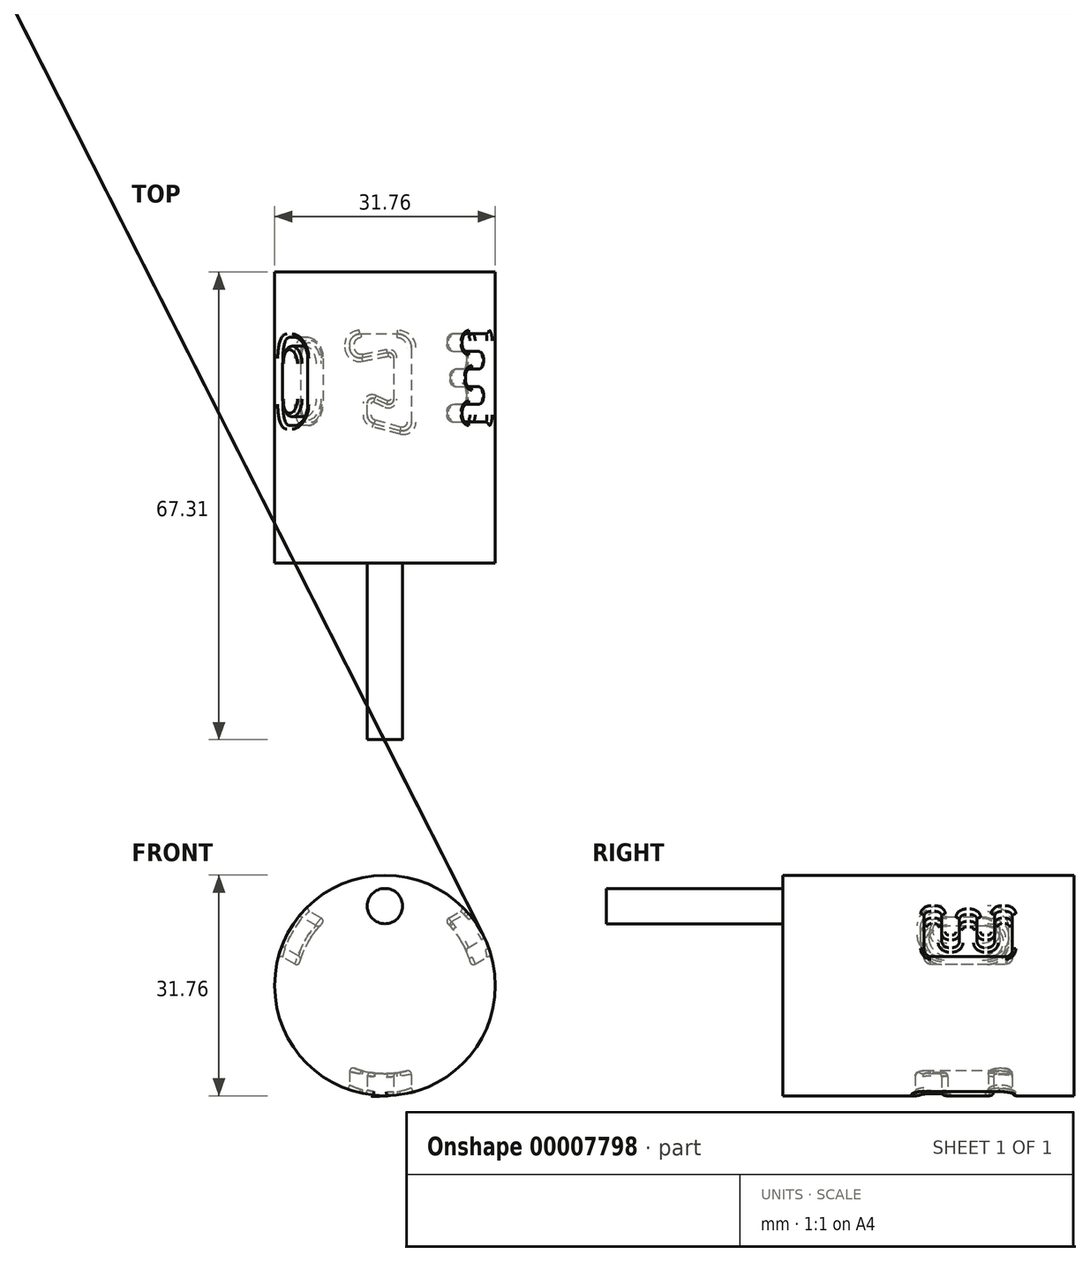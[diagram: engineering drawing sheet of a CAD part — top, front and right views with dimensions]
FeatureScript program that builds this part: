
annotation { "Feature Type Name" : "Feature", "Feature Type Description" : "" }
export const myFeature = defineFeature(function(context is Context, id is Id, definition is map)
    precondition{}
    {
        {
            var Q0;
            Q0=qCreatedBy(makeId("Front.planeOp"),FACE);
            var sketch = newSketch(context, id + "F0", { "sketchPlane" : qUnion([Q0])});
            skCircle(sketch, "E0", {"center": v(0, 0) * mm, "radius": 15.88 * mm});
            skSolve(sketch);
        }
        {
            var Q0;
            Q0 = qSketchRegion(id + "F0", true);
            extrude(context, id + "F1", {"entities" : qUnion([Q0]), "depth" : 38.1 * mm});
        }
        {
            var Q0;
            Q0=qCreatedBy(makeId("Top.planeOp"),FACE);
            var sketch = newSketch(context, id + "F2", { "sketchPlane" : qUnion([Q0])});
            skLineSegment(sketch, "E1", {"start": v(-7.62, -35.56) * mm, "end": v(0, -24.13) * mm});
            skLineSegment(sketch, "E2", {"start": v(0, -24.13) * mm, "end": v(7.62, -35.56) * mm});
            skLineSegment(sketch, "E3", {"start": v(-8.9, -5.08) * mm, "end": v(-8.9, 0) * mm});
            skLineSegment(sketch, "E4", {"start": v(-8.9, 0) * mm, "end": v(0, -5.08) * mm});
            skLineSegment(sketch, "E5", {"start": v(0, -5.08) * mm, "end": v(8.89, 0) * mm});
            skLineSegment(sketch, "E6", {"start": v(8.9, 0) * mm, "end": v(8.9, -5.08) * mm});
            skArc(sketch, "E7", {"start": v(-8.9, -15.24) * mm, "mid": v(-10.64, -25.55) * mm, "end": v(-7.62, -35.56) * mm});
            skArc(sketch, "E8", {"start": v(7.62, -35.56) * mm, "mid": v(10.64, -25.55) * mm, "end": v(8.9, -15.24) * mm});
            skArc(sketch, "E9", {"start": v(8.9, -15.24) * mm, "mid": v(12.14, -9.84) * mm, "end": v(13.97, -3.8) * mm});
            skArc(sketch, "E10", {"start": v(-13.97, -3.81) * mm, "mid": v(-12.14, -9.84) * mm, "end": v(-8.9, -15.24) * mm});
            skLineSegment(sketch, "E11", {"start": v(8.9, -5.08) * mm, "end": v(13.97, -3.8) * mm});
            skLineSegment(sketch, "E12", {"start": v(-13.97, -3.81) * mm, "end": v(-8.9, -5.08) * mm});
            skLineSegment(sketch, "E13", {"start": v(0, -24.13) * mm, "end": v(0, -5.08) * mm});
            skSolve(sketch);
        }
        {
            var Q0;
            Q0=qCreatedBy(makeId("Top.planeOp"),FACE);
            cPlane(context, id + "F3", {"entities" : qUnion([Q0]), "cplaneType" : CPlaneType.OFFSET, "offset" : 15.88 * mm, "oppositeDirection" : true, "width" : 152.4 * mm, "height" : 152.4 * mm});
        }
        {
            var Q0;
            Q0=qCreatedBy(id+"F3.planeOp",FACE);
            var sketch = newSketch(context, id + "F4", { "sketchPlane" : qUnion([Q0])});
            skLineSegment(sketch, "E14", {"start": v(3.81, -21.59) * mm, "end": v(3.8, -10.92) * mm});
            skLineSegment(sketch, "E15", {"start": v(1.78, -8.9) * mm, "end": v(-3.56, -8.9) * mm});
            skPoint(sketch, "E16.visualSharp", {"position": v(3.81, -21.59) * mm});
            skPoint(sketch, "E17.visualSharp", {"position": v(3.8, -8.9) * mm});
            skArc(sketch, "E17.filletArc", {"start": v(3.81, -10.92) * mm, "mid": v(3.21, -9.49) * mm, "end": v(1.78, -8.9) * mm});
            skLineSegment(sketch, "E18", {"start": v(-5.08, -10.41) * mm, "end": v(-5.08, -10.84) * mm});
            skLineSegment(sketch, "E19", {"start": v(-3.26, -12.34) * mm, "end": v(0.36, -11.61) * mm});
            skLineSegment(sketch, "E20", {"start": v(1.27, -12.36) * mm, "end": v(1.27, -18.29) * mm});
            skPoint(sketch, "E21.visualSharp", {"position": v(-5.08, -12.7) * mm});
            skArc(sketch, "E21.filletArc", {"start": v(-5.08, -10.84) * mm, "mid": v(-4.52, -12.02) * mm, "end": v(-3.26, -12.34) * mm});
            skPoint(sketch, "E22.visualSharp", {"position": v(-5.08, -8.9) * mm});
            skArc(sketch, "E22.filletArc", {"start": v(-3.56, -8.89) * mm, "mid": v(-4.63, -9.34) * mm, "end": v(-5.08, -10.41) * mm});
            skPoint(sketch, "E23.visualSharp", {"position": v(1.27, -11.43) * mm});
            skArc(sketch, "E23.filletArc", {"start": v(1.27, -12.36) * mm, "mid": v(1, -11.77) * mm, "end": v(0.36, -11.61) * mm});
            skLineSegment(sketch, "E24", {"start": v(2.21, -22.82) * mm, "end": v(-1.6, -21.8) * mm});
            skLineSegment(sketch, "E25", {"start": v(-2.54, -20.57) * mm, "end": v(-2.54, -18.92) * mm});
            skLineSegment(sketch, "E26", {"start": v(-1.46, -18.23) * mm, "end": v(0.2, -18.98) * mm});
            skArc(sketch, "E27.filletArc", {"start": v(2.21, -22.82) * mm, "mid": v(3.31, -22.6) * mm, "end": v(3.81, -21.59) * mm});
            skPoint(sketch, "E28.visualSharp", {"position": v(-2.54, -21.54) * mm});
            skArc(sketch, "E28.filletArc", {"start": v(-2.54, -20.57) * mm, "mid": v(-2.28, -21.34) * mm, "end": v(-1.6, -21.8) * mm});
            skPoint(sketch, "E29.visualSharp", {"position": v(-2.54, -17.73) * mm});
            skArc(sketch, "E29.filletArc", {"start": v(-1.46, -18.23) * mm, "mid": v(-2.2, -18.28) * mm, "end": v(-2.54, -18.92) * mm});
            skPoint(sketch, "E30.visualSharp", {"position": v(1.27, -19.47) * mm});
            skArc(sketch, "E30.filletArc", {"start": v(0.2, -18.98) * mm, "mid": v(0.92, -18.93) * mm, "end": v(1.27, -18.29) * mm});
            skSolve(sketch);
        }
        {
            var Q0;
            Q0 = qSketchRegion(id + "F4", true);
            extrude(context, id + "F5", {"entities" : qUnion([Q0]), "depth" : 25.4 * mm});
        }
        {
            var Q0;
            Q0=makeQuery(id+"F1.opExtrude","CAP_FACE",FACE,{"disambiguationData":[OSD([sQuery(id+"F0.wireOp",EDGE,"E0")])],"isStart":false});
            var sketch = newSketch(context, id + "F6", { "sketchPlane" : qUnion([Q0])});
            skCircle(sketch, "E31", {"center": v(0, 0) * mm, "radius": 12.7 * mm});
            skSolve(sketch);
        }
        {
            var Q0;
            Q0 = qSketchRegion(id + "F6", true);
            extrude(context, id + "F7", {"entities" : qUnion([Q0]), "oppositeDirection" : true, "depth" : 38.1 * mm});
        }
        {
            var Q0;
            Q0=makeQuery(id+"F7.opExtrude","SWEPT_BODY",BODY,{"disambiguationData":[OSD([sQuery(id+"F6.wireOp",EDGE,"E31")])]});
            var Q1;
            Q1=makeQuery(id+"F5.opExtrude","SWEPT_BODY",BODY,{"disambiguationData":[OSD([sQuery(id+"F4.wireOp",EDGE,"E14"),sQuery(id+"F4.wireOp",EDGE,"E15"),sQuery(id+"F4.wireOp",EDGE,"E17.filletArc"),sQuery(id+"F4.wireOp",EDGE,"E18"),sQuery(id+"F4.wireOp",EDGE,"E19"),sQuery(id+"F4.wireOp",EDGE,"E20"),sQuery(id+"F4.wireOp",EDGE,"E21.filletArc"),sQuery(id+"F4.wireOp",EDGE,"E22.filletArc"),sQuery(id+"F4.wireOp",EDGE,"E23.filletArc"),sQuery(id+"F4.wireOp",EDGE,"E24"),sQuery(id+"F4.wireOp",EDGE,"E25"),sQuery(id+"F4.wireOp",EDGE,"E26"),sQuery(id+"F4.wireOp",EDGE,"E27.filletArc"),sQuery(id+"F4.wireOp",EDGE,"E28.filletArc"),sQuery(id+"F4.wireOp",EDGE,"E29.filletArc"),sQuery(id+"F4.wireOp",EDGE,"E30.filletArc")])]});
            booleanBodies(context, id + "F8", {"operationType" : BooleanOperationType.SUBTRACTION, "tools" : qUnion([Q0]), "targets" : qUnion([Q1]), "keepTools" : true});
        }
        {
            var Q0;
            Q0=makeQuery(id+"F5.opExtrude","SWEPT_BODY",BODY,{"disambiguationData":[OSD([sQuery(id+"F4.wireOp",EDGE,"E14"),sQuery(id+"F4.wireOp",EDGE,"E15"),sQuery(id+"F4.wireOp",EDGE,"E17.filletArc"),sQuery(id+"F4.wireOp",EDGE,"E18"),sQuery(id+"F4.wireOp",EDGE,"E19"),sQuery(id+"F4.wireOp",EDGE,"E20"),sQuery(id+"F4.wireOp",EDGE,"E21.filletArc"),sQuery(id+"F4.wireOp",EDGE,"E22.filletArc"),sQuery(id+"F4.wireOp",EDGE,"E23.filletArc"),sQuery(id+"F4.wireOp",EDGE,"E24"),sQuery(id+"F4.wireOp",EDGE,"E25"),sQuery(id+"F4.wireOp",EDGE,"E26"),sQuery(id+"F4.wireOp",EDGE,"E27.filletArc"),sQuery(id+"F4.wireOp",EDGE,"E28.filletArc"),sQuery(id+"F4.wireOp",EDGE,"E29.filletArc"),sQuery(id+"F4.wireOp",EDGE,"E30.filletArc")])]});
            var Q1;
            Q1=makeQuery(id+"F1.opExtrude","SWEPT_BODY",BODY,{"disambiguationData":[OSD([sQuery(id+"F0.wireOp",EDGE,"E0")])]});
            booleanBodies(context, id + "F9", {"operationType" : BooleanOperationType.SUBTRACTION, "tools" : qUnion([Q0]), "targets" : qUnion([Q1])});
        }
        {
            var Q0;
            Q0=makeQuery(id+"F9.opBoolean","COPY",EDGE,{"derivedFrom":makeQuery(id+"F8.opBoolean","INTERSECT",EDGE,{"derivedFrom":[makeQuery(id+"F5.opExtrude","SWEPT_FACE",FACE,{"disambiguationData":[OSD([sQuery(id+"F4.wireOp",EDGE,"E20")])]}),makeQuery(id+"F7.opExtrude","SWEPT_FACE",FACE,{"disambiguationData":[OSD([sQuery(id+"F6.wireOp",EDGE,"E31")])]})]})});
            var Q1;
            Q1=makeQuery(id+"F9.opBoolean","COPY",EDGE,{"derivedFrom":makeQuery(id+"F8.opBoolean","INTERSECT",EDGE,{"derivedFrom":[makeQuery(id+"F5.opExtrude","SWEPT_FACE",FACE,{"disambiguationData":[OSD([sQuery(id+"F4.wireOp",EDGE,"E30.filletArc")])]}),makeQuery(id+"F7.opExtrude","SWEPT_FACE",FACE,{"disambiguationData":[OSD([sQuery(id+"F6.wireOp",EDGE,"E31")])]})]})});
            var Q2;
            Q2=makeQuery(id+"F9.opBoolean","COPY",EDGE,{"derivedFrom":makeQuery(id+"F8.opBoolean","INTERSECT",EDGE,{"derivedFrom":[makeQuery(id+"F5.opExtrude","SWEPT_FACE",FACE,{"disambiguationData":[OSD([sQuery(id+"F4.wireOp",EDGE,"E26")])]}),makeQuery(id+"F7.opExtrude","SWEPT_FACE",FACE,{"disambiguationData":[OSD([sQuery(id+"F6.wireOp",EDGE,"E31")])]})]})});
            var Q3;
            Q3=makeQuery(id+"F9.opBoolean","COPY",EDGE,{"derivedFrom":makeQuery(id+"F8.opBoolean","INTERSECT",EDGE,{"derivedFrom":[makeQuery(id+"F5.opExtrude","SWEPT_FACE",FACE,{"disambiguationData":[OSD([sQuery(id+"F4.wireOp",EDGE,"E29.filletArc")])]}),makeQuery(id+"F7.opExtrude","SWEPT_FACE",FACE,{"disambiguationData":[OSD([sQuery(id+"F6.wireOp",EDGE,"E31")])]})]})});
            var Q4;
            Q4=makeQuery(id+"F9.opBoolean","COPY",EDGE,{"derivedFrom":makeQuery(id+"F8.opBoolean","INTERSECT",EDGE,{"derivedFrom":[makeQuery(id+"F5.opExtrude","SWEPT_FACE",FACE,{"disambiguationData":[OSD([sQuery(id+"F4.wireOp",EDGE,"E25")])]}),makeQuery(id+"F7.opExtrude","SWEPT_FACE",FACE,{"disambiguationData":[OSD([sQuery(id+"F6.wireOp",EDGE,"E31")])]})]})});
            var Q5;
            Q5=makeQuery(id+"F9.opBoolean","COPY",EDGE,{"derivedFrom":makeQuery(id+"F8.opBoolean","INTERSECT",EDGE,{"derivedFrom":[makeQuery(id+"F5.opExtrude","SWEPT_FACE",FACE,{"disambiguationData":[OSD([sQuery(id+"F4.wireOp",EDGE,"E28.filletArc")])]}),makeQuery(id+"F7.opExtrude","SWEPT_FACE",FACE,{"disambiguationData":[OSD([sQuery(id+"F6.wireOp",EDGE,"E31")])]})]})});
            var Q6;
            Q6=makeQuery(id+"F9.opBoolean","COPY",EDGE,{"derivedFrom":makeQuery(id+"F8.opBoolean","INTERSECT",EDGE,{"derivedFrom":[makeQuery(id+"F5.opExtrude","SWEPT_FACE",FACE,{"disambiguationData":[OSD([sQuery(id+"F4.wireOp",EDGE,"E24")])]}),makeQuery(id+"F7.opExtrude","SWEPT_FACE",FACE,{"disambiguationData":[OSD([sQuery(id+"F6.wireOp",EDGE,"E31")])]})]})});
            var Q7;
            Q7=makeQuery(id+"F9.opBoolean","COPY",EDGE,{"derivedFrom":makeQuery(id+"F8.opBoolean","INTERSECT",EDGE,{"derivedFrom":[makeQuery(id+"F5.opExtrude","SWEPT_FACE",FACE,{"disambiguationData":[OSD([sQuery(id+"F4.wireOp",EDGE,"E27.filletArc")])]}),makeQuery(id+"F7.opExtrude","SWEPT_FACE",FACE,{"disambiguationData":[OSD([sQuery(id+"F6.wireOp",EDGE,"E31")])]})]})});
            var Q8;
            Q8=makeQuery(id+"F9.opBoolean","COPY",EDGE,{"derivedFrom":makeQuery(id+"F8.opBoolean","INTERSECT",EDGE,{"derivedFrom":[makeQuery(id+"F5.opExtrude","SWEPT_FACE",FACE,{"disambiguationData":[OSD([sQuery(id+"F4.wireOp",EDGE,"E14")])]}),makeQuery(id+"F7.opExtrude","SWEPT_FACE",FACE,{"disambiguationData":[OSD([sQuery(id+"F6.wireOp",EDGE,"E31")])]})]})});
            var Q9;
            Q9=makeQuery(id+"F9.opBoolean","COPY",EDGE,{"derivedFrom":makeQuery(id+"F8.opBoolean","INTERSECT",EDGE,{"derivedFrom":[makeQuery(id+"F5.opExtrude","SWEPT_FACE",FACE,{"disambiguationData":[OSD([sQuery(id+"F4.wireOp",EDGE,"E17.filletArc")])]}),makeQuery(id+"F7.opExtrude","SWEPT_FACE",FACE,{"disambiguationData":[OSD([sQuery(id+"F6.wireOp",EDGE,"E31")])]})]})});
            var Q10;
            Q10=makeQuery(id+"F9.opBoolean","COPY",EDGE,{"derivedFrom":makeQuery(id+"F8.opBoolean","INTERSECT",EDGE,{"derivedFrom":[makeQuery(id+"F5.opExtrude","SWEPT_FACE",FACE,{"disambiguationData":[OSD([sQuery(id+"F4.wireOp",EDGE,"E15")])]}),makeQuery(id+"F7.opExtrude","SWEPT_FACE",FACE,{"disambiguationData":[OSD([sQuery(id+"F6.wireOp",EDGE,"E31")])]})]})});
            var Q11;
            Q11=makeQuery(id+"F9.opBoolean","COPY",EDGE,{"derivedFrom":makeQuery(id+"F8.opBoolean","INTERSECT",EDGE,{"derivedFrom":[makeQuery(id+"F5.opExtrude","SWEPT_FACE",FACE,{"disambiguationData":[OSD([sQuery(id+"F4.wireOp",EDGE,"E22.filletArc")])]}),makeQuery(id+"F7.opExtrude","SWEPT_FACE",FACE,{"disambiguationData":[OSD([sQuery(id+"F6.wireOp",EDGE,"E31")])]})]})});
            var Q12;
            Q12=makeQuery(id+"F9.opBoolean","COPY",EDGE,{"derivedFrom":makeQuery(id+"F8.opBoolean","INTERSECT",EDGE,{"derivedFrom":[makeQuery(id+"F5.opExtrude","SWEPT_FACE",FACE,{"disambiguationData":[OSD([sQuery(id+"F4.wireOp",EDGE,"E18")])]}),makeQuery(id+"F7.opExtrude","SWEPT_FACE",FACE,{"disambiguationData":[OSD([sQuery(id+"F6.wireOp",EDGE,"E31")])]})]})});
            var Q13;
            Q13=makeQuery(id+"F9.opBoolean","COPY",EDGE,{"derivedFrom":makeQuery(id+"F8.opBoolean","INTERSECT",EDGE,{"derivedFrom":[makeQuery(id+"F5.opExtrude","SWEPT_FACE",FACE,{"disambiguationData":[OSD([sQuery(id+"F4.wireOp",EDGE,"E21.filletArc")])]}),makeQuery(id+"F7.opExtrude","SWEPT_FACE",FACE,{"disambiguationData":[OSD([sQuery(id+"F6.wireOp",EDGE,"E31")])]})]})});
            var Q14;
            Q14=makeQuery(id+"F9.opBoolean","COPY",EDGE,{"derivedFrom":makeQuery(id+"F8.opBoolean","INTERSECT",EDGE,{"derivedFrom":[makeQuery(id+"F5.opExtrude","SWEPT_FACE",FACE,{"disambiguationData":[OSD([sQuery(id+"F4.wireOp",EDGE,"E19")])]}),makeQuery(id+"F7.opExtrude","SWEPT_FACE",FACE,{"disambiguationData":[OSD([sQuery(id+"F6.wireOp",EDGE,"E31")])]})]})});
            var Q15;
            Q15=makeQuery(id+"F9.opBoolean","COPY",EDGE,{"derivedFrom":makeQuery(id+"F8.opBoolean","INTERSECT",EDGE,{"derivedFrom":[makeQuery(id+"F5.opExtrude","SWEPT_FACE",FACE,{"disambiguationData":[OSD([sQuery(id+"F4.wireOp",EDGE,"E23.filletArc")])]}),makeQuery(id+"F7.opExtrude","SWEPT_FACE",FACE,{"disambiguationData":[OSD([sQuery(id+"F6.wireOp",EDGE,"E31")])]})]})});
            fillet(context, id + "F10", {"entities" : qUnion([Q0, Q1, Q2, Q3, Q4, Q5, Q6, Q7, Q8, Q9, Q10, Q11, Q12, Q13, Q14, Q15]), "radius" : 0.5 * mm, "tangentPropagation" : true, "allowEdgeOverflow" : false});
        }
        {
            var Q0;
            Q0=makeQuery(id+"F9.opBoolean","INTERSECT",EDGE,{"derivedFrom":[makeQuery(id+"F1.opExtrude","SWEPT_FACE",FACE,{"disambiguationData":[OSD([sQuery(id+"F0.wireOp",EDGE,"E0")])]}),makeQuery(id+"F5.opExtrude","SWEPT_FACE",FACE,{"disambiguationData":[OSD([sQuery(id+"F4.wireOp",EDGE,"E14")])]})]});
            var Q1;
            Q1=makeQuery(id+"F9.opBoolean","INTERSECT",EDGE,{"derivedFrom":[makeQuery(id+"F1.opExtrude","SWEPT_FACE",FACE,{"disambiguationData":[OSD([sQuery(id+"F0.wireOp",EDGE,"E0")])]}),makeQuery(id+"F5.opExtrude","SWEPT_FACE",FACE,{"disambiguationData":[OSD([sQuery(id+"F4.wireOp",EDGE,"E27.filletArc")])]})]});
            var Q2;
            Q2=makeQuery(id+"F9.opBoolean","INTERSECT",EDGE,{"derivedFrom":[makeQuery(id+"F1.opExtrude","SWEPT_FACE",FACE,{"disambiguationData":[OSD([sQuery(id+"F0.wireOp",EDGE,"E0")])]}),makeQuery(id+"F5.opExtrude","SWEPT_FACE",FACE,{"disambiguationData":[OSD([sQuery(id+"F4.wireOp",EDGE,"E24")])]})]});
            var Q3;
            Q3=makeQuery(id+"F9.opBoolean","INTERSECT",EDGE,{"derivedFrom":[makeQuery(id+"F1.opExtrude","SWEPT_FACE",FACE,{"disambiguationData":[OSD([sQuery(id+"F0.wireOp",EDGE,"E0")])]}),makeQuery(id+"F5.opExtrude","SWEPT_FACE",FACE,{"disambiguationData":[OSD([sQuery(id+"F4.wireOp",EDGE,"E28.filletArc")])]})]});
            var Q4;
            Q4=makeQuery(id+"F9.opBoolean","INTERSECT",EDGE,{"derivedFrom":[makeQuery(id+"F1.opExtrude","SWEPT_FACE",FACE,{"disambiguationData":[OSD([sQuery(id+"F0.wireOp",EDGE,"E0")])]}),makeQuery(id+"F5.opExtrude","SWEPT_FACE",FACE,{"disambiguationData":[OSD([sQuery(id+"F4.wireOp",EDGE,"E25")])]})]});
            var Q5;
            Q5=makeQuery(id+"F9.opBoolean","INTERSECT",EDGE,{"derivedFrom":[makeQuery(id+"F1.opExtrude","SWEPT_FACE",FACE,{"disambiguationData":[OSD([sQuery(id+"F0.wireOp",EDGE,"E0")])]}),makeQuery(id+"F5.opExtrude","SWEPT_FACE",FACE,{"disambiguationData":[OSD([sQuery(id+"F4.wireOp",EDGE,"E29.filletArc")])]})]});
            var Q6;
            Q6=makeQuery(id+"F9.opBoolean","INTERSECT",EDGE,{"derivedFrom":[makeQuery(id+"F1.opExtrude","SWEPT_FACE",FACE,{"disambiguationData":[OSD([sQuery(id+"F0.wireOp",EDGE,"E0")])]}),makeQuery(id+"F5.opExtrude","SWEPT_FACE",FACE,{"disambiguationData":[OSD([sQuery(id+"F4.wireOp",EDGE,"E26")])]})]});
            var Q7;
            Q7=makeQuery(id+"F9.opBoolean","INTERSECT",EDGE,{"derivedFrom":[makeQuery(id+"F1.opExtrude","SWEPT_FACE",FACE,{"disambiguationData":[OSD([sQuery(id+"F0.wireOp",EDGE,"E0")])]}),makeQuery(id+"F5.opExtrude","SWEPT_FACE",FACE,{"disambiguationData":[OSD([sQuery(id+"F4.wireOp",EDGE,"E30.filletArc")])]})]});
            var Q8;
            Q8=makeQuery(id+"F9.opBoolean","INTERSECT",EDGE,{"derivedFrom":[makeQuery(id+"F1.opExtrude","SWEPT_FACE",FACE,{"disambiguationData":[OSD([sQuery(id+"F0.wireOp",EDGE,"E0")])]}),makeQuery(id+"F5.opExtrude","SWEPT_FACE",FACE,{"disambiguationData":[OSD([sQuery(id+"F4.wireOp",EDGE,"E20")])]})]});
            var Q9;
            Q9=makeQuery(id+"F9.opBoolean","INTERSECT",EDGE,{"derivedFrom":[makeQuery(id+"F1.opExtrude","SWEPT_FACE",FACE,{"disambiguationData":[OSD([sQuery(id+"F0.wireOp",EDGE,"E0")])]}),makeQuery(id+"F5.opExtrude","SWEPT_FACE",FACE,{"disambiguationData":[OSD([sQuery(id+"F4.wireOp",EDGE,"E19")])]})]});
            var Q10;
            Q10=makeQuery(id+"F9.opBoolean","INTERSECT",EDGE,{"derivedFrom":[makeQuery(id+"F1.opExtrude","SWEPT_FACE",FACE,{"disambiguationData":[OSD([sQuery(id+"F0.wireOp",EDGE,"E0")])]}),makeQuery(id+"F5.opExtrude","SWEPT_FACE",FACE,{"disambiguationData":[OSD([sQuery(id+"F4.wireOp",EDGE,"E23.filletArc")])]})]});
            var Q11;
            Q11=makeQuery(id+"F9.opBoolean","INTERSECT",EDGE,{"derivedFrom":[makeQuery(id+"F1.opExtrude","SWEPT_FACE",FACE,{"disambiguationData":[OSD([sQuery(id+"F0.wireOp",EDGE,"E0")])]}),makeQuery(id+"F5.opExtrude","SWEPT_FACE",FACE,{"disambiguationData":[OSD([sQuery(id+"F4.wireOp",EDGE,"E21.filletArc")])]})]});
            var Q12;
            Q12=makeQuery(id+"F9.opBoolean","INTERSECT",EDGE,{"derivedFrom":[makeQuery(id+"F1.opExtrude","SWEPT_FACE",FACE,{"disambiguationData":[OSD([sQuery(id+"F0.wireOp",EDGE,"E0")])]}),makeQuery(id+"F5.opExtrude","SWEPT_FACE",FACE,{"disambiguationData":[OSD([sQuery(id+"F4.wireOp",EDGE,"E18")])]})]});
            var Q13;
            Q13=makeQuery(id+"F9.opBoolean","INTERSECT",EDGE,{"derivedFrom":[makeQuery(id+"F1.opExtrude","SWEPT_FACE",FACE,{"disambiguationData":[OSD([sQuery(id+"F0.wireOp",EDGE,"E0")])]}),makeQuery(id+"F5.opExtrude","SWEPT_FACE",FACE,{"disambiguationData":[OSD([sQuery(id+"F4.wireOp",EDGE,"E22.filletArc")])]})]});
            var Q14;
            Q14=makeQuery(id+"F9.opBoolean","INTERSECT",EDGE,{"derivedFrom":[makeQuery(id+"F1.opExtrude","SWEPT_FACE",FACE,{"disambiguationData":[OSD([sQuery(id+"F0.wireOp",EDGE,"E0")])]}),makeQuery(id+"F5.opExtrude","SWEPT_FACE",FACE,{"disambiguationData":[OSD([sQuery(id+"F4.wireOp",EDGE,"E15")])]})]});
            var Q15;
            Q15=makeQuery(id+"F9.opBoolean","INTERSECT",EDGE,{"derivedFrom":[makeQuery(id+"F1.opExtrude","SWEPT_FACE",FACE,{"disambiguationData":[OSD([sQuery(id+"F0.wireOp",EDGE,"E0")])]}),makeQuery(id+"F5.opExtrude","SWEPT_FACE",FACE,{"disambiguationData":[OSD([sQuery(id+"F4.wireOp",EDGE,"E17.filletArc")])]})]});
            fillet(context, id + "F11", {"entities" : qUnion([Q0, Q1, Q2, Q3, Q4, Q5, Q6, Q7, Q8, Q9, Q10, Q11, Q12, Q13, Q14, Q15]), "radius" : 0.5 * mm, "tangentPropagation" : true, "allowEdgeOverflow" : false});
        }
        {
            var Q0;
            Q0=makeQuery(id+"F2.imprint","IMPRINT",FACE,{"disambiguationData":[TD([[makeQuery(id+"F2.imprint","IMPRINT",EDGE,{"derivedFrom":sQuery(id+"F2.wireOp",EDGE,"E2")}),1.0]])]});
            var Q1;
            Q1=sQuery(id+"F2.wireOp",EDGE,"E1");
            var Q2;
            Q2=sQuery(id+"F2.wireOp",EDGE,"E7");
            var Q3;
            Q3=sQuery(id+"F2.wireOp",EDGE,"E10");
            var Q4;
            Q4=sQuery(id+"F2.wireOp",EDGE,"E12");
            var Q5;
            Q5=sQuery(id+"F2.wireOp",EDGE,"E3");
            var Q6;
            Q6=sQuery(id+"F2.wireOp",EDGE,"E4");
            var Q7;
            Q7=sQuery(id+"F2.wireOp",EDGE,"E13");
            revolve(context, id + "F12", {"bodyType" : ToolBodyType.SURFACE, "entities" : qUnion([Q0]), "surfaceEntities" : qUnion([Q1, Q2, Q3, Q4, Q5, Q6]), "axis" : qUnion([Q7]), "revolveType" : RevolveType.ONE_DIRECTION, "angle" : 120 * degree});
        }
        {
            var Q0;
            Q0=sQuery(id+"F2.wireOp",EDGE,"E13");
            cPlane(context, id + "F13", {"entities" : qUnion([Q0]), "cplaneType" : CPlaneType.LINE_ANGLE, "offset" : 152.4 * mm, "angle" : 120 * degree, "width" : 152.4 * mm, "height" : 152.4 * mm});
        }
        {
            var Q0;
            Q0=qCreatedBy(id+"F13.planeOp",FACE);
            cPlane(context, id + "F14", {"entities" : qUnion([Q0]), "cplaneType" : CPlaneType.OFFSET, "offset" : 15.88 * mm, "oppositeDirection" : true, "width" : 152.4 * mm, "height" : 152.4 * mm});
        }
        {
            var Q0;
            Q0=qCreatedBy(id+"F14.planeOp",FACE);
            var sketch = newSketch(context, id + "F15", { "sketchPlane" : qUnion([Q0])});
            skLineSegment(sketch, "E32", {"start": v(-19.05, 3.8) * mm, "end": v(-12.45, 3.8) * mm});
            skLineSegment(sketch, "E33", {"start": v(-9.4, 0.76) * mm, "end": v(-9.4, -0.76) * mm});
            skLineSegment(sketch, "E34", {"start": v(-12.45, -3.81) * mm, "end": v(-19.05, -3.81) * mm});
            skLineSegment(sketch, "E35", {"start": v(-22.1, -0.76) * mm, "end": v(-22.1, 0.76) * mm});
            skPoint(sketch, "E36.visualSharp", {"position": v(-22.1, 3.8) * mm});
            skArc(sketch, "E36.filletArc", {"start": v(-19.05, 3.8) * mm, "mid": v(-21.2, 2.92) * mm, "end": v(-22.1, 0.76) * mm});
            skPoint(sketch, "E37.visualSharp", {"position": v(-22.1, -3.81) * mm});
            skArc(sketch, "E37.filletArc", {"start": v(-22.1, -0.76) * mm, "mid": v(-21.2, -2.92) * mm, "end": v(-19.05, -3.81) * mm});
            skPoint(sketch, "E38.visualSharp", {"position": v(-9.4, 3.8) * mm});
            skArc(sketch, "E38.filletArc", {"start": v(-9.4, 0.76) * mm, "mid": v(-10.3, 2.92) * mm, "end": v(-12.45, 3.8) * mm});
            skPoint(sketch, "E39.visualSharp", {"position": v(-9.4, -3.81) * mm});
            skArc(sketch, "E39.filletArc", {"start": v(-12.45, -3.81) * mm, "mid": v(-10.3, -2.92) * mm, "end": v(-9.4, -0.76) * mm});
            skLineSegment(sketch, "E40", {"start": v(-18.29, 2.54) * mm, "end": v(-13.2, 2.54) * mm});
            skLineSegment(sketch, "E41", {"start": v(-10.67, 0) * mm, "end": v(-10.67, 0) * mm});
            skLineSegment(sketch, "E42", {"start": v(-13.2, -2.54) * mm, "end": v(-18.29, -2.54) * mm});
            skLineSegment(sketch, "E43", {"start": v(-20.83, 0) * mm, "end": v(-20.83, 0) * mm});
            skPoint(sketch, "E44.visualSharp", {"position": v(-20.83, 2.54) * mm});
            skArc(sketch, "E44.filletArc", {"start": v(-18.29, 2.54) * mm, "mid": v(-20.08, 1.8) * mm, "end": v(-20.83, 0) * mm});
            skPoint(sketch, "E45.visualSharp", {"position": v(-20.83, -2.54) * mm});
            skArc(sketch, "E45.filletArc", {"start": v(-20.83, 0) * mm, "mid": v(-20.08, -1.8) * mm, "end": v(-18.29, -2.54) * mm});
            skPoint(sketch, "E46.visualSharp", {"position": v(-10.67, 2.54) * mm});
            skArc(sketch, "E46.filletArc", {"start": v(-10.67, 0) * mm, "mid": v(-11.41, 1.8) * mm, "end": v(-13.2, 2.54) * mm});
            skPoint(sketch, "E47.visualSharp", {"position": v(-10.67, -2.54) * mm});
            skArc(sketch, "E47.filletArc", {"start": v(-13.2, -2.54) * mm, "mid": v(-11.41, -1.8) * mm, "end": v(-10.67, 0) * mm});
            skSolve(sketch);
        }
        {
            var Q0;
            Q0 = qSketchRegion(id + "F15", true);
            extrude(context, id + "F16", {"entities" : qUnion([Q0]), "depth" : 25.4 * mm});
        }
        {
            var Q0;
            Q0=makeQuery(id+"F7.opExtrude","SWEPT_BODY",BODY,{"disambiguationData":[OSD([sQuery(id+"F6.wireOp",EDGE,"E31")])]});
            var Q1;
            Q1=makeQuery(id+"F16.opExtrude","SWEPT_BODY",BODY,{"disambiguationData":[OSD([sQuery(id+"F15.wireOp",EDGE,"E32"),sQuery(id+"F15.wireOp",EDGE,"E33"),sQuery(id+"F15.wireOp",EDGE,"E34"),sQuery(id+"F15.wireOp",EDGE,"E35"),sQuery(id+"F15.wireOp",EDGE,"E36.filletArc"),sQuery(id+"F15.wireOp",EDGE,"E37.filletArc"),sQuery(id+"F15.wireOp",EDGE,"E38.filletArc"),sQuery(id+"F15.wireOp",EDGE,"E39.filletArc"),sQuery(id+"F15.wireOp",EDGE,"E40"),sQuery(id+"F15.wireOp",EDGE,"E42"),sQuery(id+"F15.wireOp",EDGE,"E44.filletArc"),sQuery(id+"F15.wireOp",EDGE,"E45.filletArc"),sQuery(id+"F15.wireOp",EDGE,"E46.filletArc"),sQuery(id+"F15.wireOp",EDGE,"E47.filletArc")])]});
            booleanBodies(context, id + "F17", {"operationType" : BooleanOperationType.SUBTRACTION, "tools" : qUnion([Q0]), "targets" : qUnion([Q1]), "keepTools" : true});
        }
        {
            var Q0;
            Q0=makeQuery(id+"F16.opExtrude","SWEPT_BODY",BODY,{"disambiguationData":[OSD([sQuery(id+"F15.wireOp",EDGE,"E32"),sQuery(id+"F15.wireOp",EDGE,"E33"),sQuery(id+"F15.wireOp",EDGE,"E34"),sQuery(id+"F15.wireOp",EDGE,"E35"),sQuery(id+"F15.wireOp",EDGE,"E36.filletArc"),sQuery(id+"F15.wireOp",EDGE,"E37.filletArc"),sQuery(id+"F15.wireOp",EDGE,"E38.filletArc"),sQuery(id+"F15.wireOp",EDGE,"E39.filletArc"),sQuery(id+"F15.wireOp",EDGE,"E40"),sQuery(id+"F15.wireOp",EDGE,"E42"),sQuery(id+"F15.wireOp",EDGE,"E44.filletArc"),sQuery(id+"F15.wireOp",EDGE,"E45.filletArc"),sQuery(id+"F15.wireOp",EDGE,"E46.filletArc"),sQuery(id+"F15.wireOp",EDGE,"E47.filletArc")])]});
            var Q1;
            Q1=makeQuery(id+"F1.opExtrude","SWEPT_BODY",BODY,{"disambiguationData":[OSD([sQuery(id+"F0.wireOp",EDGE,"E0")])]});
            booleanBodies(context, id + "F18", {"operationType" : BooleanOperationType.SUBTRACTION, "tools" : qUnion([Q0]), "targets" : qUnion([Q1])});
        }
        {
            var Q0;
            Q0=makeQuery(id+"F18.opBoolean","INTERSECT",EDGE,{"derivedFrom":[makeQuery(id+"F1.opExtrude","SWEPT_FACE",FACE,{"disambiguationData":[OSD([sQuery(id+"F0.wireOp",EDGE,"E0")])]}),makeQuery(id+"F16.opExtrude","SWEPT_FACE",FACE,{"disambiguationData":[OSD([sQuery(id+"F15.wireOp",EDGE,"E36.filletArc")])]})]});
            var Q1;
            Q1=makeQuery(id+"F18.opBoolean","INTERSECT",EDGE,{"derivedFrom":[makeQuery(id+"F1.opExtrude","SWEPT_FACE",FACE,{"disambiguationData":[OSD([sQuery(id+"F0.wireOp",EDGE,"E0")])]}),makeQuery(id+"F16.opExtrude","SWEPT_FACE",FACE,{"disambiguationData":[OSD([sQuery(id+"F15.wireOp",EDGE,"E35")])]})]});
            var Q2;
            Q2=makeQuery(id+"F18.opBoolean","INTERSECT",EDGE,{"derivedFrom":[makeQuery(id+"F1.opExtrude","SWEPT_FACE",FACE,{"disambiguationData":[OSD([sQuery(id+"F0.wireOp",EDGE,"E0")])]}),makeQuery(id+"F16.opExtrude","SWEPT_FACE",FACE,{"disambiguationData":[OSD([sQuery(id+"F15.wireOp",EDGE,"E37.filletArc")])]})]});
            var Q3;
            Q3=makeQuery(id+"F18.opBoolean","INTERSECT",EDGE,{"derivedFrom":[makeQuery(id+"F1.opExtrude","SWEPT_FACE",FACE,{"disambiguationData":[OSD([sQuery(id+"F0.wireOp",EDGE,"E0")])]}),makeQuery(id+"F16.opExtrude","SWEPT_FACE",FACE,{"disambiguationData":[OSD([sQuery(id+"F15.wireOp",EDGE,"E34")])]})]});
            var Q4;
            Q4=makeQuery(id+"F18.opBoolean","INTERSECT",EDGE,{"derivedFrom":[makeQuery(id+"F1.opExtrude","SWEPT_FACE",FACE,{"disambiguationData":[OSD([sQuery(id+"F0.wireOp",EDGE,"E0")])]}),makeQuery(id+"F16.opExtrude","SWEPT_FACE",FACE,{"disambiguationData":[OSD([sQuery(id+"F15.wireOp",EDGE,"E39.filletArc")])]})]});
            var Q5;
            Q5=makeQuery(id+"F18.opBoolean","INTERSECT",EDGE,{"derivedFrom":[makeQuery(id+"F1.opExtrude","SWEPT_FACE",FACE,{"disambiguationData":[OSD([sQuery(id+"F0.wireOp",EDGE,"E0")])]}),makeQuery(id+"F16.opExtrude","SWEPT_FACE",FACE,{"disambiguationData":[OSD([sQuery(id+"F15.wireOp",EDGE,"E33")])]})]});
            var Q6;
            Q6=makeQuery(id+"F18.opBoolean","INTERSECT",EDGE,{"derivedFrom":[makeQuery(id+"F1.opExtrude","SWEPT_FACE",FACE,{"disambiguationData":[OSD([sQuery(id+"F0.wireOp",EDGE,"E0")])]}),makeQuery(id+"F16.opExtrude","SWEPT_FACE",FACE,{"disambiguationData":[OSD([sQuery(id+"F15.wireOp",EDGE,"E38.filletArc")])]})]});
            var Q7;
            Q7=makeQuery(id+"F18.opBoolean","INTERSECT",EDGE,{"derivedFrom":[makeQuery(id+"F1.opExtrude","SWEPT_FACE",FACE,{"disambiguationData":[OSD([sQuery(id+"F0.wireOp",EDGE,"E0")])]}),makeQuery(id+"F16.opExtrude","SWEPT_FACE",FACE,{"disambiguationData":[OSD([sQuery(id+"F15.wireOp",EDGE,"E32")])]})]});
            var Q8;
            Q8=makeQuery(id+"F18.opBoolean","INTERSECT",EDGE,{"derivedFrom":[makeQuery(id+"F1.opExtrude","SWEPT_FACE",FACE,{"disambiguationData":[OSD([sQuery(id+"F0.wireOp",EDGE,"E0")])]}),makeQuery(id+"F16.opExtrude","SWEPT_FACE",FACE,{"disambiguationData":[OSD([sQuery(id+"F15.wireOp",EDGE,"E44.filletArc"),sQuery(id+"F15.wireOp",EDGE,"E45.filletArc")])]})]});
            var Q9;
            Q9=makeQuery(id+"F18.opBoolean","INTERSECT",EDGE,{"derivedFrom":[makeQuery(id+"F1.opExtrude","SWEPT_FACE",FACE,{"disambiguationData":[OSD([sQuery(id+"F0.wireOp",EDGE,"E0")])]}),makeQuery(id+"F16.opExtrude","SWEPT_FACE",FACE,{"disambiguationData":[OSD([sQuery(id+"F15.wireOp",EDGE,"E40")])]})]});
            var Q10;
            Q10=makeQuery(id+"F18.opBoolean","INTERSECT",EDGE,{"derivedFrom":[makeQuery(id+"F1.opExtrude","SWEPT_FACE",FACE,{"disambiguationData":[OSD([sQuery(id+"F0.wireOp",EDGE,"E0")])]}),makeQuery(id+"F16.opExtrude","SWEPT_FACE",FACE,{"disambiguationData":[OSD([sQuery(id+"F15.wireOp",EDGE,"E46.filletArc"),sQuery(id+"F15.wireOp",EDGE,"E47.filletArc")])]})]});
            var Q11;
            Q11=makeQuery(id+"F18.opBoolean","INTERSECT",EDGE,{"derivedFrom":[makeQuery(id+"F1.opExtrude","SWEPT_FACE",FACE,{"disambiguationData":[OSD([sQuery(id+"F0.wireOp",EDGE,"E0")])]}),makeQuery(id+"F16.opExtrude","SWEPT_FACE",FACE,{"disambiguationData":[OSD([sQuery(id+"F15.wireOp",EDGE,"E42")])]})]});
            fillet(context, id + "F19", {"entities" : qUnion([Q0, Q1, Q2, Q3, Q4, Q5, Q6, Q7, Q8, Q9, Q10, Q11]), "radius" : 0.5 * mm, "tangentPropagation" : true, "allowEdgeOverflow" : false});
        }
        {
            var Q0;
            Q0=makeQuery(id+"F18.opBoolean","COPY",EDGE,{"derivedFrom":makeQuery(id+"F17.opBoolean","INTERSECT",EDGE,{"derivedFrom":[makeQuery(id+"F7.opExtrude","SWEPT_FACE",FACE,{"disambiguationData":[OSD([sQuery(id+"F6.wireOp",EDGE,"E31")])]}),makeQuery(id+"F16.opExtrude","SWEPT_FACE",FACE,{"disambiguationData":[OSD([sQuery(id+"F15.wireOp",EDGE,"E36.filletArc")])]})]})});
            var Q1;
            Q1=makeQuery(id+"F18.opBoolean","COPY",EDGE,{"derivedFrom":makeQuery(id+"F17.opBoolean","INTERSECT",EDGE,{"derivedFrom":[makeQuery(id+"F7.opExtrude","SWEPT_FACE",FACE,{"disambiguationData":[OSD([sQuery(id+"F6.wireOp",EDGE,"E31")])]}),makeQuery(id+"F16.opExtrude","SWEPT_FACE",FACE,{"disambiguationData":[OSD([sQuery(id+"F15.wireOp",EDGE,"E35")])]})]})});
            var Q2;
            Q2=makeQuery(id+"F18.opBoolean","COPY",EDGE,{"derivedFrom":makeQuery(id+"F17.opBoolean","INTERSECT",EDGE,{"derivedFrom":[makeQuery(id+"F7.opExtrude","SWEPT_FACE",FACE,{"disambiguationData":[OSD([sQuery(id+"F6.wireOp",EDGE,"E31")])]}),makeQuery(id+"F16.opExtrude","SWEPT_FACE",FACE,{"disambiguationData":[OSD([sQuery(id+"F15.wireOp",EDGE,"E37.filletArc")])]})]})});
            var Q3;
            Q3=makeQuery(id+"F18.opBoolean","COPY",EDGE,{"derivedFrom":makeQuery(id+"F17.opBoolean","INTERSECT",EDGE,{"derivedFrom":[makeQuery(id+"F7.opExtrude","SWEPT_FACE",FACE,{"disambiguationData":[OSD([sQuery(id+"F6.wireOp",EDGE,"E31")])]}),makeQuery(id+"F16.opExtrude","SWEPT_FACE",FACE,{"disambiguationData":[OSD([sQuery(id+"F15.wireOp",EDGE,"E32")])]})]})});
            var Q4;
            Q4=makeQuery(id+"F18.opBoolean","COPY",EDGE,{"derivedFrom":makeQuery(id+"F17.opBoolean","INTERSECT",EDGE,{"derivedFrom":[makeQuery(id+"F7.opExtrude","SWEPT_FACE",FACE,{"disambiguationData":[OSD([sQuery(id+"F6.wireOp",EDGE,"E31")])]}),makeQuery(id+"F16.opExtrude","SWEPT_FACE",FACE,{"disambiguationData":[OSD([sQuery(id+"F15.wireOp",EDGE,"E38.filletArc")])]})]})});
            var Q5;
            Q5=makeQuery(id+"F18.opBoolean","COPY",EDGE,{"derivedFrom":makeQuery(id+"F17.opBoolean","INTERSECT",EDGE,{"derivedFrom":[makeQuery(id+"F7.opExtrude","SWEPT_FACE",FACE,{"disambiguationData":[OSD([sQuery(id+"F6.wireOp",EDGE,"E31")])]}),makeQuery(id+"F16.opExtrude","SWEPT_FACE",FACE,{"disambiguationData":[OSD([sQuery(id+"F15.wireOp",EDGE,"E33")])]})]})});
            var Q6;
            Q6=makeQuery(id+"F18.opBoolean","COPY",EDGE,{"derivedFrom":makeQuery(id+"F17.opBoolean","INTERSECT",EDGE,{"derivedFrom":[makeQuery(id+"F7.opExtrude","SWEPT_FACE",FACE,{"disambiguationData":[OSD([sQuery(id+"F6.wireOp",EDGE,"E31")])]}),makeQuery(id+"F16.opExtrude","SWEPT_FACE",FACE,{"disambiguationData":[OSD([sQuery(id+"F15.wireOp",EDGE,"E39.filletArc")])]})]})});
            var Q7;
            Q7=makeQuery(id+"F18.opBoolean","COPY",EDGE,{"derivedFrom":makeQuery(id+"F17.opBoolean","INTERSECT",EDGE,{"derivedFrom":[makeQuery(id+"F7.opExtrude","SWEPT_FACE",FACE,{"disambiguationData":[OSD([sQuery(id+"F6.wireOp",EDGE,"E31")])]}),makeQuery(id+"F16.opExtrude","SWEPT_FACE",FACE,{"disambiguationData":[OSD([sQuery(id+"F15.wireOp",EDGE,"E34")])]})]})});
            var Q8;
            Q8=makeQuery(id+"F18.opBoolean","COPY",EDGE,{"derivedFrom":makeQuery(id+"F17.opBoolean","INTERSECT",EDGE,{"derivedFrom":[makeQuery(id+"F7.opExtrude","SWEPT_FACE",FACE,{"disambiguationData":[OSD([sQuery(id+"F6.wireOp",EDGE,"E31")])]}),makeQuery(id+"F16.opExtrude","SWEPT_FACE",FACE,{"disambiguationData":[OSD([sQuery(id+"F15.wireOp",EDGE,"E40")])]})]})});
            var Q9;
            Q9=makeQuery(id+"F18.opBoolean","COPY",EDGE,{"derivedFrom":makeQuery(id+"F17.opBoolean","INTERSECT",EDGE,{"derivedFrom":[makeQuery(id+"F7.opExtrude","SWEPT_FACE",FACE,{"disambiguationData":[OSD([sQuery(id+"F6.wireOp",EDGE,"E31")])]}),makeQuery(id+"F16.opExtrude","SWEPT_FACE",FACE,{"disambiguationData":[OSD([sQuery(id+"F15.wireOp",EDGE,"E46.filletArc"),sQuery(id+"F15.wireOp",EDGE,"E47.filletArc")])]})]})});
            var Q10;
            Q10=makeQuery(id+"F18.opBoolean","COPY",EDGE,{"derivedFrom":makeQuery(id+"F17.opBoolean","INTERSECT",EDGE,{"derivedFrom":[makeQuery(id+"F7.opExtrude","SWEPT_FACE",FACE,{"disambiguationData":[OSD([sQuery(id+"F6.wireOp",EDGE,"E31")])]}),makeQuery(id+"F16.opExtrude","SWEPT_FACE",FACE,{"disambiguationData":[OSD([sQuery(id+"F15.wireOp",EDGE,"E44.filletArc"),sQuery(id+"F15.wireOp",EDGE,"E45.filletArc")])]})]})});
            var Q11;
            Q11=makeQuery(id+"F18.opBoolean","COPY",EDGE,{"derivedFrom":makeQuery(id+"F17.opBoolean","INTERSECT",EDGE,{"derivedFrom":[makeQuery(id+"F7.opExtrude","SWEPT_FACE",FACE,{"disambiguationData":[OSD([sQuery(id+"F6.wireOp",EDGE,"E31")])]}),makeQuery(id+"F16.opExtrude","SWEPT_FACE",FACE,{"disambiguationData":[OSD([sQuery(id+"F15.wireOp",EDGE,"E42")])]})]})});
            fillet(context, id + "F20", {"entities" : qUnion([Q0, Q1, Q2, Q3, Q4, Q5, Q6, Q7, Q8, Q9, Q10, Q11]), "radius" : 0.5 * mm, "tangentPropagation" : true, "allowEdgeOverflow" : false});
        }
        {
            var Q0;
            Q0=sQuery(id+"F2.wireOp",EDGE,"E13");
            cPlane(context, id + "F21", {"entities" : qUnion([Q0]), "cplaneType" : CPlaneType.LINE_ANGLE, "offset" : 152.4 * mm, "angle" : 240 * degree, "width" : 152.4 * mm, "height" : 152.4 * mm});
        }
        {
            var Q0;
            Q0=qCreatedBy(id+"F21.planeOp",FACE);
            cPlane(context, id + "F22", {"entities" : qUnion([Q0]), "cplaneType" : CPlaneType.OFFSET, "offset" : 15.88 * mm, "oppositeDirection" : true, "width" : 152.4 * mm, "height" : 152.4 * mm});
        }
        {
            var Q0;
            Q0=qCreatedBy(id+"F22.planeOp",FACE);
            var sketch = newSketch(context, id + "F23", { "sketchPlane" : qUnion([Q0])});
            skLineSegment(sketch, "E48", {"start": v(21.59, -2.8) * mm, "end": v(21.59, 2.8) * mm});
            skLineSegment(sketch, "E49", {"start": v(20.57, 3.8) * mm, "end": v(20.07, 3.8) * mm});
            skLineSegment(sketch, "E50", {"start": v(19.05, 2.8) * mm, "end": v(19.05, -0.25) * mm});
            skLineSegment(sketch, "E51", {"start": v(18.03, -1.27) * mm, "end": v(17.53, -1.27) * mm});
            skLineSegment(sketch, "E52", {"start": v(16.5, -0.25) * mm, "end": v(16.5, 2.16) * mm});
            skLineSegment(sketch, "E53", {"start": v(15.5, 3.17) * mm, "end": v(14.99, 3.17) * mm});
            skLineSegment(sketch, "E54", {"start": v(13.97, 2.16) * mm, "end": v(13.97, -0.25) * mm});
            skLineSegment(sketch, "E55", {"start": v(12.95, -1.27) * mm, "end": v(12.45, -1.27) * mm});
            skLineSegment(sketch, "E56", {"start": v(11.43, -0.25) * mm, "end": v(11.43, 2.8) * mm});
            skLineSegment(sketch, "E57", {"start": v(10.41, 3.81) * mm, "end": v(9.9, 3.81) * mm});
            skLineSegment(sketch, "E58", {"start": v(8.89, 2.8) * mm, "end": v(8.89, -2.8) * mm});
            skLineSegment(sketch, "E59", {"start": v(9.9, -3.8) * mm, "end": v(20.57, -3.81) * mm});
            skPoint(sketch, "E60.visualSharp", {"position": v(21.59, -3.81) * mm});
            skArc(sketch, "E60.filletArc", {"start": v(20.57, -3.81) * mm, "mid": v(21.3, -3.51) * mm, "end": v(21.59, -2.8) * mm});
            skPoint(sketch, "E61.visualSharp", {"position": v(21.59, 3.8) * mm});
            skArc(sketch, "E61.filletArc", {"start": v(21.59, 2.8) * mm, "mid": v(21.3, 3.51) * mm, "end": v(20.57, 3.81) * mm});
            skPoint(sketch, "E62.visualSharp", {"position": v(19.05, 3.8) * mm});
            skArc(sketch, "E62.filletArc", {"start": v(20.07, 3.8) * mm, "mid": v(19.35, 3.51) * mm, "end": v(19.05, 2.8) * mm});
            skPoint(sketch, "E63.visualSharp", {"position": v(19.05, -1.27) * mm});
            skArc(sketch, "E63.filletArc", {"start": v(18.03, -1.27) * mm, "mid": v(18.75, -0.97) * mm, "end": v(19.05, -0.25) * mm});
            skPoint(sketch, "E64.visualSharp", {"position": v(16.5, -1.27) * mm});
            skArc(sketch, "E64.filletArc", {"start": v(16.5, -0.25) * mm, "mid": v(16.8, -0.97) * mm, "end": v(17.53, -1.27) * mm});
            skPoint(sketch, "E65.visualSharp", {"position": v(16.5, 3.17) * mm});
            skArc(sketch, "E65.filletArc", {"start": v(16.5, 2.16) * mm, "mid": v(16.21, 2.88) * mm, "end": v(15.5, 3.17) * mm});
            skPoint(sketch, "E66.visualSharp", {"position": v(13.97, 3.17) * mm});
            skArc(sketch, "E66.filletArc", {"start": v(14.99, 3.17) * mm, "mid": v(14.27, 2.88) * mm, "end": v(13.97, 2.16) * mm});
            skPoint(sketch, "E67.visualSharp", {"position": v(13.97, -1.27) * mm});
            skArc(sketch, "E67.filletArc", {"start": v(12.95, -1.27) * mm, "mid": v(13.67, -0.97) * mm, "end": v(13.97, -0.25) * mm});
            skPoint(sketch, "E68.visualSharp", {"position": v(11.43, -1.27) * mm});
            skArc(sketch, "E68.filletArc", {"start": v(11.43, -0.25) * mm, "mid": v(11.73, -0.97) * mm, "end": v(12.45, -1.27) * mm});
            skPoint(sketch, "E69.visualSharp", {"position": v(11.43, 3.81) * mm});
            skArc(sketch, "E69.filletArc", {"start": v(11.43, 2.8) * mm, "mid": v(11.13, 3.51) * mm, "end": v(10.41, 3.81) * mm});
            skPoint(sketch, "E70.visualSharp", {"position": v(8.89, 3.81) * mm});
            skArc(sketch, "E70.filletArc", {"start": v(9.9, 3.81) * mm, "mid": v(9.19, 3.51) * mm, "end": v(8.89, 2.8) * mm});
            skPoint(sketch, "E71.visualSharp", {"position": v(8.89, -3.8) * mm});
            skArc(sketch, "E71.filletArc", {"start": v(8.89, -2.8) * mm, "mid": v(9.19, -3.51) * mm, "end": v(9.9, -3.81) * mm});
            skSolve(sketch);
        }
        {
            var Q0;
            Q0 = qSketchRegion(id + "F23", true);
            extrude(context, id + "F24", {"entities" : qUnion([Q0]), "depth" : 25.4 * mm});
        }
        {
            var Q0;
            Q0=makeQuery(id+"F7.opExtrude","SWEPT_BODY",BODY,{"disambiguationData":[OSD([sQuery(id+"F6.wireOp",EDGE,"E31")])]});
            var Q1;
            Q1=makeQuery(id+"F24.opExtrude","SWEPT_BODY",BODY,{"disambiguationData":[OSD([sQuery(id+"F23.wireOp",EDGE,"E48"),sQuery(id+"F23.wireOp",EDGE,"E49"),sQuery(id+"F23.wireOp",EDGE,"E50"),sQuery(id+"F23.wireOp",EDGE,"E51"),sQuery(id+"F23.wireOp",EDGE,"E52"),sQuery(id+"F23.wireOp",EDGE,"E53"),sQuery(id+"F23.wireOp",EDGE,"E54"),sQuery(id+"F23.wireOp",EDGE,"E55"),sQuery(id+"F23.wireOp",EDGE,"E56"),sQuery(id+"F23.wireOp",EDGE,"E57"),sQuery(id+"F23.wireOp",EDGE,"E58"),sQuery(id+"F23.wireOp",EDGE,"E59"),sQuery(id+"F23.wireOp",EDGE,"E60.filletArc"),sQuery(id+"F23.wireOp",EDGE,"E61.filletArc"),sQuery(id+"F23.wireOp",EDGE,"E62.filletArc"),sQuery(id+"F23.wireOp",EDGE,"E63.filletArc"),sQuery(id+"F23.wireOp",EDGE,"E64.filletArc"),sQuery(id+"F23.wireOp",EDGE,"E65.filletArc"),sQuery(id+"F23.wireOp",EDGE,"E66.filletArc"),sQuery(id+"F23.wireOp",EDGE,"E67.filletArc"),sQuery(id+"F23.wireOp",EDGE,"E68.filletArc"),sQuery(id+"F23.wireOp",EDGE,"E69.filletArc"),sQuery(id+"F23.wireOp",EDGE,"E70.filletArc"),sQuery(id+"F23.wireOp",EDGE,"E71.filletArc")])]});
            booleanBodies(context, id + "F25", {"operationType" : BooleanOperationType.SUBTRACTION, "tools" : qUnion([Q0]), "targets" : qUnion([Q1]), "keepTools" : true});
        }
        {
            var Q0;
            Q0=makeQuery(id+"F24.opExtrude","SWEPT_BODY",BODY,{"disambiguationData":[OSD([sQuery(id+"F23.wireOp",EDGE,"E48"),sQuery(id+"F23.wireOp",EDGE,"E49"),sQuery(id+"F23.wireOp",EDGE,"E50"),sQuery(id+"F23.wireOp",EDGE,"E51"),sQuery(id+"F23.wireOp",EDGE,"E52"),sQuery(id+"F23.wireOp",EDGE,"E53"),sQuery(id+"F23.wireOp",EDGE,"E54"),sQuery(id+"F23.wireOp",EDGE,"E55"),sQuery(id+"F23.wireOp",EDGE,"E56"),sQuery(id+"F23.wireOp",EDGE,"E57"),sQuery(id+"F23.wireOp",EDGE,"E58"),sQuery(id+"F23.wireOp",EDGE,"E59"),sQuery(id+"F23.wireOp",EDGE,"E60.filletArc"),sQuery(id+"F23.wireOp",EDGE,"E61.filletArc"),sQuery(id+"F23.wireOp",EDGE,"E62.filletArc"),sQuery(id+"F23.wireOp",EDGE,"E63.filletArc"),sQuery(id+"F23.wireOp",EDGE,"E64.filletArc"),sQuery(id+"F23.wireOp",EDGE,"E65.filletArc"),sQuery(id+"F23.wireOp",EDGE,"E66.filletArc"),sQuery(id+"F23.wireOp",EDGE,"E67.filletArc"),sQuery(id+"F23.wireOp",EDGE,"E68.filletArc"),sQuery(id+"F23.wireOp",EDGE,"E69.filletArc"),sQuery(id+"F23.wireOp",EDGE,"E70.filletArc"),sQuery(id+"F23.wireOp",EDGE,"E71.filletArc")])]});
            var Q1;
            Q1=makeQuery(id+"F1.opExtrude","SWEPT_BODY",BODY,{"disambiguationData":[OSD([sQuery(id+"F0.wireOp",EDGE,"E0")])]});
            booleanBodies(context, id + "F26", {"operationType" : BooleanOperationType.SUBTRACTION, "tools" : qUnion([Q0]), "targets" : qUnion([Q1])});
        }
        {
            var Q0;
            {var subQ0=sQuery(id+"F0.wireOp",EDGE,"E0");Q0=makeQuery(id+"F26.opBoolean","INTERSECT",EDGE,{"derivedFrom":[makeQuery(id+"F18.opBoolean","SPLIT",FACE,{"disambiguationData":[TD([makeQuery(id+"F1.opExtrude","CAP_FACE",FACE,{"disambiguationData":[OSD([subQ0])],"isStart":true})])],"derivedFrom":makeQuery(id+"F1.opExtrude","SWEPT_FACE",FACE,{"disambiguationData":[OSD([subQ0])]})}),makeQuery(id+"F24.opExtrude","SWEPT_FACE",FACE,{"disambiguationData":[OSD([sQuery(id+"F23.wireOp",EDGE,"E59")])]})]});}
            var Q1;
            {var subQ0=sQuery(id+"F0.wireOp",EDGE,"E0");Q1=makeQuery(id+"F26.opBoolean","INTERSECT",EDGE,{"derivedFrom":[makeQuery(id+"F18.opBoolean","SPLIT",FACE,{"disambiguationData":[TD([makeQuery(id+"F1.opExtrude","CAP_FACE",FACE,{"disambiguationData":[OSD([subQ0])],"isStart":true})])],"derivedFrom":makeQuery(id+"F1.opExtrude","SWEPT_FACE",FACE,{"disambiguationData":[OSD([subQ0])]})}),makeQuery(id+"F24.opExtrude","SWEPT_FACE",FACE,{"disambiguationData":[OSD([sQuery(id+"F23.wireOp",EDGE,"E60.filletArc")])]})]});}
            var Q2;
            {var subQ0=sQuery(id+"F0.wireOp",EDGE,"E0");Q2=makeQuery(id+"F26.opBoolean","INTERSECT",EDGE,{"derivedFrom":[makeQuery(id+"F18.opBoolean","SPLIT",FACE,{"disambiguationData":[TD([makeQuery(id+"F1.opExtrude","CAP_FACE",FACE,{"disambiguationData":[OSD([subQ0])],"isStart":true})])],"derivedFrom":makeQuery(id+"F1.opExtrude","SWEPT_FACE",FACE,{"disambiguationData":[OSD([subQ0])]})}),makeQuery(id+"F24.opExtrude","SWEPT_FACE",FACE,{"disambiguationData":[OSD([sQuery(id+"F23.wireOp",EDGE,"E48")])]})]});}
            var Q3;
            {var subQ0=sQuery(id+"F0.wireOp",EDGE,"E0");Q3=makeQuery(id+"F26.opBoolean","INTERSECT",EDGE,{"derivedFrom":[makeQuery(id+"F18.opBoolean","SPLIT",FACE,{"disambiguationData":[TD([makeQuery(id+"F1.opExtrude","CAP_FACE",FACE,{"disambiguationData":[OSD([subQ0])],"isStart":true})])],"derivedFrom":makeQuery(id+"F1.opExtrude","SWEPT_FACE",FACE,{"disambiguationData":[OSD([subQ0])]})}),makeQuery(id+"F24.opExtrude","SWEPT_FACE",FACE,{"disambiguationData":[OSD([sQuery(id+"F23.wireOp",EDGE,"E61.filletArc")])]})]});}
            var Q4;
            {var subQ0=sQuery(id+"F0.wireOp",EDGE,"E0");Q4=makeQuery(id+"F26.opBoolean","INTERSECT",EDGE,{"derivedFrom":[makeQuery(id+"F18.opBoolean","SPLIT",FACE,{"disambiguationData":[TD([makeQuery(id+"F1.opExtrude","CAP_FACE",FACE,{"disambiguationData":[OSD([subQ0])],"isStart":true})])],"derivedFrom":makeQuery(id+"F1.opExtrude","SWEPT_FACE",FACE,{"disambiguationData":[OSD([subQ0])]})}),makeQuery(id+"F24.opExtrude","SWEPT_FACE",FACE,{"disambiguationData":[OSD([sQuery(id+"F23.wireOp",EDGE,"E49")])]})]});}
            var Q5;
            {var subQ0=sQuery(id+"F0.wireOp",EDGE,"E0");Q5=makeQuery(id+"F26.opBoolean","INTERSECT",EDGE,{"derivedFrom":[makeQuery(id+"F18.opBoolean","SPLIT",FACE,{"disambiguationData":[TD([makeQuery(id+"F1.opExtrude","CAP_FACE",FACE,{"disambiguationData":[OSD([subQ0])],"isStart":true})])],"derivedFrom":makeQuery(id+"F1.opExtrude","SWEPT_FACE",FACE,{"disambiguationData":[OSD([subQ0])]})}),makeQuery(id+"F24.opExtrude","SWEPT_FACE",FACE,{"disambiguationData":[OSD([sQuery(id+"F23.wireOp",EDGE,"E62.filletArc")])]})]});}
            var Q6;
            {var subQ0=sQuery(id+"F0.wireOp",EDGE,"E0");Q6=makeQuery(id+"F26.opBoolean","INTERSECT",EDGE,{"derivedFrom":[makeQuery(id+"F18.opBoolean","SPLIT",FACE,{"disambiguationData":[TD([makeQuery(id+"F1.opExtrude","CAP_FACE",FACE,{"disambiguationData":[OSD([subQ0])],"isStart":true})])],"derivedFrom":makeQuery(id+"F1.opExtrude","SWEPT_FACE",FACE,{"disambiguationData":[OSD([subQ0])]})}),makeQuery(id+"F24.opExtrude","SWEPT_FACE",FACE,{"disambiguationData":[OSD([sQuery(id+"F23.wireOp",EDGE,"E50")])]})]});}
            var Q7;
            {var subQ0=sQuery(id+"F0.wireOp",EDGE,"E0");Q7=makeQuery(id+"F26.opBoolean","INTERSECT",EDGE,{"derivedFrom":[makeQuery(id+"F18.opBoolean","SPLIT",FACE,{"disambiguationData":[TD([makeQuery(id+"F1.opExtrude","CAP_FACE",FACE,{"disambiguationData":[OSD([subQ0])],"isStart":true})])],"derivedFrom":makeQuery(id+"F1.opExtrude","SWEPT_FACE",FACE,{"disambiguationData":[OSD([subQ0])]})}),makeQuery(id+"F24.opExtrude","SWEPT_FACE",FACE,{"disambiguationData":[OSD([sQuery(id+"F23.wireOp",EDGE,"E63.filletArc")])]})]});}
            var Q8;
            {var subQ0=sQuery(id+"F0.wireOp",EDGE,"E0");Q8=makeQuery(id+"F26.opBoolean","INTERSECT",EDGE,{"derivedFrom":[makeQuery(id+"F18.opBoolean","SPLIT",FACE,{"disambiguationData":[TD([makeQuery(id+"F1.opExtrude","CAP_FACE",FACE,{"disambiguationData":[OSD([subQ0])],"isStart":true})])],"derivedFrom":makeQuery(id+"F1.opExtrude","SWEPT_FACE",FACE,{"disambiguationData":[OSD([subQ0])]})}),makeQuery(id+"F24.opExtrude","SWEPT_FACE",FACE,{"disambiguationData":[OSD([sQuery(id+"F23.wireOp",EDGE,"E64.filletArc")])]})]});}
            var Q9;
            {var subQ0=sQuery(id+"F0.wireOp",EDGE,"E0");Q9=makeQuery(id+"F26.opBoolean","INTERSECT",EDGE,{"derivedFrom":[makeQuery(id+"F18.opBoolean","SPLIT",FACE,{"disambiguationData":[TD([makeQuery(id+"F1.opExtrude","CAP_FACE",FACE,{"disambiguationData":[OSD([subQ0])],"isStart":true})])],"derivedFrom":makeQuery(id+"F1.opExtrude","SWEPT_FACE",FACE,{"disambiguationData":[OSD([subQ0])]})}),makeQuery(id+"F24.opExtrude","SWEPT_FACE",FACE,{"disambiguationData":[OSD([sQuery(id+"F23.wireOp",EDGE,"E51")])]})]});}
            var Q10;
            {var subQ0=sQuery(id+"F0.wireOp",EDGE,"E0");Q10=makeQuery(id+"F26.opBoolean","INTERSECT",EDGE,{"derivedFrom":[makeQuery(id+"F18.opBoolean","SPLIT",FACE,{"disambiguationData":[TD([makeQuery(id+"F1.opExtrude","CAP_FACE",FACE,{"disambiguationData":[OSD([subQ0])],"isStart":true})])],"derivedFrom":makeQuery(id+"F1.opExtrude","SWEPT_FACE",FACE,{"disambiguationData":[OSD([subQ0])]})}),makeQuery(id+"F24.opExtrude","SWEPT_FACE",FACE,{"disambiguationData":[OSD([sQuery(id+"F23.wireOp",EDGE,"E52")])]})]});}
            var Q11;
            {var subQ0=sQuery(id+"F0.wireOp",EDGE,"E0");Q11=makeQuery(id+"F26.opBoolean","INTERSECT",EDGE,{"derivedFrom":[makeQuery(id+"F18.opBoolean","SPLIT",FACE,{"disambiguationData":[TD([makeQuery(id+"F1.opExtrude","CAP_FACE",FACE,{"disambiguationData":[OSD([subQ0])],"isStart":true})])],"derivedFrom":makeQuery(id+"F1.opExtrude","SWEPT_FACE",FACE,{"disambiguationData":[OSD([subQ0])]})}),makeQuery(id+"F24.opExtrude","SWEPT_FACE",FACE,{"disambiguationData":[OSD([sQuery(id+"F23.wireOp",EDGE,"E65.filletArc")])]})]});}
            var Q12;
            {var subQ0=sQuery(id+"F0.wireOp",EDGE,"E0");Q12=makeQuery(id+"F26.opBoolean","INTERSECT",EDGE,{"derivedFrom":[makeQuery(id+"F18.opBoolean","SPLIT",FACE,{"disambiguationData":[TD([makeQuery(id+"F1.opExtrude","CAP_FACE",FACE,{"disambiguationData":[OSD([subQ0])],"isStart":true})])],"derivedFrom":makeQuery(id+"F1.opExtrude","SWEPT_FACE",FACE,{"disambiguationData":[OSD([subQ0])]})}),makeQuery(id+"F24.opExtrude","SWEPT_FACE",FACE,{"disambiguationData":[OSD([sQuery(id+"F23.wireOp",EDGE,"E53")])]})]});}
            var Q13;
            {var subQ0=sQuery(id+"F0.wireOp",EDGE,"E0");Q13=makeQuery(id+"F26.opBoolean","INTERSECT",EDGE,{"derivedFrom":[makeQuery(id+"F18.opBoolean","SPLIT",FACE,{"disambiguationData":[TD([makeQuery(id+"F1.opExtrude","CAP_FACE",FACE,{"disambiguationData":[OSD([subQ0])],"isStart":true})])],"derivedFrom":makeQuery(id+"F1.opExtrude","SWEPT_FACE",FACE,{"disambiguationData":[OSD([subQ0])]})}),makeQuery(id+"F24.opExtrude","SWEPT_FACE",FACE,{"disambiguationData":[OSD([sQuery(id+"F23.wireOp",EDGE,"E66.filletArc")])]})]});}
            var Q14;
            {var subQ0=sQuery(id+"F0.wireOp",EDGE,"E0");Q14=makeQuery(id+"F26.opBoolean","INTERSECT",EDGE,{"derivedFrom":[makeQuery(id+"F18.opBoolean","SPLIT",FACE,{"disambiguationData":[TD([makeQuery(id+"F1.opExtrude","CAP_FACE",FACE,{"disambiguationData":[OSD([subQ0])],"isStart":true})])],"derivedFrom":makeQuery(id+"F1.opExtrude","SWEPT_FACE",FACE,{"disambiguationData":[OSD([subQ0])]})}),makeQuery(id+"F24.opExtrude","SWEPT_FACE",FACE,{"disambiguationData":[OSD([sQuery(id+"F23.wireOp",EDGE,"E54")])]})]});}
            var Q15;
            {var subQ0=sQuery(id+"F0.wireOp",EDGE,"E0");Q15=makeQuery(id+"F26.opBoolean","INTERSECT",EDGE,{"derivedFrom":[makeQuery(id+"F18.opBoolean","SPLIT",FACE,{"disambiguationData":[TD([makeQuery(id+"F1.opExtrude","CAP_FACE",FACE,{"disambiguationData":[OSD([subQ0])],"isStart":true})])],"derivedFrom":makeQuery(id+"F1.opExtrude","SWEPT_FACE",FACE,{"disambiguationData":[OSD([subQ0])]})}),makeQuery(id+"F24.opExtrude","SWEPT_FACE",FACE,{"disambiguationData":[OSD([sQuery(id+"F23.wireOp",EDGE,"E67.filletArc")])]})]});}
            var Q16;
            {var subQ0=sQuery(id+"F0.wireOp",EDGE,"E0");Q16=makeQuery(id+"F26.opBoolean","INTERSECT",EDGE,{"derivedFrom":[makeQuery(id+"F18.opBoolean","SPLIT",FACE,{"disambiguationData":[TD([makeQuery(id+"F1.opExtrude","CAP_FACE",FACE,{"disambiguationData":[OSD([subQ0])],"isStart":true})])],"derivedFrom":makeQuery(id+"F1.opExtrude","SWEPT_FACE",FACE,{"disambiguationData":[OSD([subQ0])]})}),makeQuery(id+"F24.opExtrude","SWEPT_FACE",FACE,{"disambiguationData":[OSD([sQuery(id+"F23.wireOp",EDGE,"E55")])]})]});}
            var Q17;
            {var subQ0=sQuery(id+"F0.wireOp",EDGE,"E0");Q17=makeQuery(id+"F26.opBoolean","INTERSECT",EDGE,{"derivedFrom":[makeQuery(id+"F18.opBoolean","SPLIT",FACE,{"disambiguationData":[TD([makeQuery(id+"F1.opExtrude","CAP_FACE",FACE,{"disambiguationData":[OSD([subQ0])],"isStart":true})])],"derivedFrom":makeQuery(id+"F1.opExtrude","SWEPT_FACE",FACE,{"disambiguationData":[OSD([subQ0])]})}),makeQuery(id+"F24.opExtrude","SWEPT_FACE",FACE,{"disambiguationData":[OSD([sQuery(id+"F23.wireOp",EDGE,"E68.filletArc")])]})]});}
            var Q18;
            {var subQ0=sQuery(id+"F0.wireOp",EDGE,"E0");Q18=makeQuery(id+"F26.opBoolean","INTERSECT",EDGE,{"derivedFrom":[makeQuery(id+"F18.opBoolean","SPLIT",FACE,{"disambiguationData":[TD([makeQuery(id+"F1.opExtrude","CAP_FACE",FACE,{"disambiguationData":[OSD([subQ0])],"isStart":true})])],"derivedFrom":makeQuery(id+"F1.opExtrude","SWEPT_FACE",FACE,{"disambiguationData":[OSD([subQ0])]})}),makeQuery(id+"F24.opExtrude","SWEPT_FACE",FACE,{"disambiguationData":[OSD([sQuery(id+"F23.wireOp",EDGE,"E56")])]})]});}
            var Q19;
            {var subQ0=sQuery(id+"F0.wireOp",EDGE,"E0");Q19=makeQuery(id+"F26.opBoolean","INTERSECT",EDGE,{"derivedFrom":[makeQuery(id+"F18.opBoolean","SPLIT",FACE,{"disambiguationData":[TD([makeQuery(id+"F1.opExtrude","CAP_FACE",FACE,{"disambiguationData":[OSD([subQ0])],"isStart":true})])],"derivedFrom":makeQuery(id+"F1.opExtrude","SWEPT_FACE",FACE,{"disambiguationData":[OSD([subQ0])]})}),makeQuery(id+"F24.opExtrude","SWEPT_FACE",FACE,{"disambiguationData":[OSD([sQuery(id+"F23.wireOp",EDGE,"E69.filletArc")])]})]});}
            var Q20;
            {var subQ0=sQuery(id+"F0.wireOp",EDGE,"E0");Q20=makeQuery(id+"F26.opBoolean","INTERSECT",EDGE,{"derivedFrom":[makeQuery(id+"F18.opBoolean","SPLIT",FACE,{"disambiguationData":[TD([makeQuery(id+"F1.opExtrude","CAP_FACE",FACE,{"disambiguationData":[OSD([subQ0])],"isStart":true})])],"derivedFrom":makeQuery(id+"F1.opExtrude","SWEPT_FACE",FACE,{"disambiguationData":[OSD([subQ0])]})}),makeQuery(id+"F24.opExtrude","SWEPT_FACE",FACE,{"disambiguationData":[OSD([sQuery(id+"F23.wireOp",EDGE,"E57")])]})]});}
            var Q21;
            {var subQ0=sQuery(id+"F0.wireOp",EDGE,"E0");Q21=makeQuery(id+"F26.opBoolean","INTERSECT",EDGE,{"derivedFrom":[makeQuery(id+"F18.opBoolean","SPLIT",FACE,{"disambiguationData":[TD([makeQuery(id+"F1.opExtrude","CAP_FACE",FACE,{"disambiguationData":[OSD([subQ0])],"isStart":true})])],"derivedFrom":makeQuery(id+"F1.opExtrude","SWEPT_FACE",FACE,{"disambiguationData":[OSD([subQ0])]})}),makeQuery(id+"F24.opExtrude","SWEPT_FACE",FACE,{"disambiguationData":[OSD([sQuery(id+"F23.wireOp",EDGE,"E70.filletArc")])]})]});}
            var Q22;
            {var subQ0=sQuery(id+"F0.wireOp",EDGE,"E0");Q22=makeQuery(id+"F26.opBoolean","INTERSECT",EDGE,{"derivedFrom":[makeQuery(id+"F18.opBoolean","SPLIT",FACE,{"disambiguationData":[TD([makeQuery(id+"F1.opExtrude","CAP_FACE",FACE,{"disambiguationData":[OSD([subQ0])],"isStart":true})])],"derivedFrom":makeQuery(id+"F1.opExtrude","SWEPT_FACE",FACE,{"disambiguationData":[OSD([subQ0])]})}),makeQuery(id+"F24.opExtrude","SWEPT_FACE",FACE,{"disambiguationData":[OSD([sQuery(id+"F23.wireOp",EDGE,"E58")])]})]});}
            var Q23;
            {var subQ0=sQuery(id+"F0.wireOp",EDGE,"E0");Q23=makeQuery(id+"F26.opBoolean","INTERSECT",EDGE,{"derivedFrom":[makeQuery(id+"F18.opBoolean","SPLIT",FACE,{"disambiguationData":[TD([makeQuery(id+"F1.opExtrude","CAP_FACE",FACE,{"disambiguationData":[OSD([subQ0])],"isStart":true})])],"derivedFrom":makeQuery(id+"F1.opExtrude","SWEPT_FACE",FACE,{"disambiguationData":[OSD([subQ0])]})}),makeQuery(id+"F24.opExtrude","SWEPT_FACE",FACE,{"disambiguationData":[OSD([sQuery(id+"F23.wireOp",EDGE,"E71.filletArc")])]})]});}
            var Q24;
            Q24=makeQuery(id+"F26.opBoolean","COPY",EDGE,{"derivedFrom":makeQuery(id+"F25.opBoolean","INTERSECT",EDGE,{"derivedFrom":[makeQuery(id+"F7.opExtrude","SWEPT_FACE",FACE,{"disambiguationData":[OSD([sQuery(id+"F6.wireOp",EDGE,"E31")])]}),makeQuery(id+"F24.opExtrude","SWEPT_FACE",FACE,{"disambiguationData":[OSD([sQuery(id+"F23.wireOp",EDGE,"E59")])]})]})});
            var Q25;
            Q25=makeQuery(id+"F26.opBoolean","COPY",EDGE,{"derivedFrom":makeQuery(id+"F25.opBoolean","INTERSECT",EDGE,{"derivedFrom":[makeQuery(id+"F7.opExtrude","SWEPT_FACE",FACE,{"disambiguationData":[OSD([sQuery(id+"F6.wireOp",EDGE,"E31")])]}),makeQuery(id+"F24.opExtrude","SWEPT_FACE",FACE,{"disambiguationData":[OSD([sQuery(id+"F23.wireOp",EDGE,"E60.filletArc")])]})]})});
            var Q26;
            Q26=makeQuery(id+"F26.opBoolean","COPY",EDGE,{"derivedFrom":makeQuery(id+"F25.opBoolean","INTERSECT",EDGE,{"derivedFrom":[makeQuery(id+"F7.opExtrude","SWEPT_FACE",FACE,{"disambiguationData":[OSD([sQuery(id+"F6.wireOp",EDGE,"E31")])]}),makeQuery(id+"F24.opExtrude","SWEPT_FACE",FACE,{"disambiguationData":[OSD([sQuery(id+"F23.wireOp",EDGE,"E48")])]})]})});
            var Q27;
            Q27=makeQuery(id+"F26.opBoolean","COPY",EDGE,{"derivedFrom":makeQuery(id+"F25.opBoolean","INTERSECT",EDGE,{"derivedFrom":[makeQuery(id+"F7.opExtrude","SWEPT_FACE",FACE,{"disambiguationData":[OSD([sQuery(id+"F6.wireOp",EDGE,"E31")])]}),makeQuery(id+"F24.opExtrude","SWEPT_FACE",FACE,{"disambiguationData":[OSD([sQuery(id+"F23.wireOp",EDGE,"E61.filletArc")])]})]})});
            var Q28;
            Q28=makeQuery(id+"F26.opBoolean","COPY",EDGE,{"derivedFrom":makeQuery(id+"F25.opBoolean","INTERSECT",EDGE,{"derivedFrom":[makeQuery(id+"F7.opExtrude","SWEPT_FACE",FACE,{"disambiguationData":[OSD([sQuery(id+"F6.wireOp",EDGE,"E31")])]}),makeQuery(id+"F24.opExtrude","SWEPT_FACE",FACE,{"disambiguationData":[OSD([sQuery(id+"F23.wireOp",EDGE,"E49")])]})]})});
            var Q29;
            Q29=makeQuery(id+"F26.opBoolean","COPY",EDGE,{"derivedFrom":makeQuery(id+"F25.opBoolean","INTERSECT",EDGE,{"derivedFrom":[makeQuery(id+"F7.opExtrude","SWEPT_FACE",FACE,{"disambiguationData":[OSD([sQuery(id+"F6.wireOp",EDGE,"E31")])]}),makeQuery(id+"F24.opExtrude","SWEPT_FACE",FACE,{"disambiguationData":[OSD([sQuery(id+"F23.wireOp",EDGE,"E62.filletArc")])]})]})});
            var Q30;
            Q30=makeQuery(id+"F26.opBoolean","COPY",EDGE,{"derivedFrom":makeQuery(id+"F25.opBoolean","INTERSECT",EDGE,{"derivedFrom":[makeQuery(id+"F7.opExtrude","SWEPT_FACE",FACE,{"disambiguationData":[OSD([sQuery(id+"F6.wireOp",EDGE,"E31")])]}),makeQuery(id+"F24.opExtrude","SWEPT_FACE",FACE,{"disambiguationData":[OSD([sQuery(id+"F23.wireOp",EDGE,"E63.filletArc")])]})]})});
            var Q31;
            Q31=makeQuery(id+"F26.opBoolean","COPY",EDGE,{"derivedFrom":makeQuery(id+"F25.opBoolean","INTERSECT",EDGE,{"derivedFrom":[makeQuery(id+"F7.opExtrude","SWEPT_FACE",FACE,{"disambiguationData":[OSD([sQuery(id+"F6.wireOp",EDGE,"E31")])]}),makeQuery(id+"F24.opExtrude","SWEPT_FACE",FACE,{"disambiguationData":[OSD([sQuery(id+"F23.wireOp",EDGE,"E51")])]})]})});
            var Q32;
            Q32=makeQuery(id+"F26.opBoolean","COPY",EDGE,{"derivedFrom":makeQuery(id+"F25.opBoolean","INTERSECT",EDGE,{"derivedFrom":[makeQuery(id+"F7.opExtrude","SWEPT_FACE",FACE,{"disambiguationData":[OSD([sQuery(id+"F6.wireOp",EDGE,"E31")])]}),makeQuery(id+"F24.opExtrude","SWEPT_FACE",FACE,{"disambiguationData":[OSD([sQuery(id+"F23.wireOp",EDGE,"E64.filletArc")])]})]})});
            var Q33;
            Q33=makeQuery(id+"F26.opBoolean","COPY",EDGE,{"derivedFrom":makeQuery(id+"F25.opBoolean","INTERSECT",EDGE,{"derivedFrom":[makeQuery(id+"F7.opExtrude","SWEPT_FACE",FACE,{"disambiguationData":[OSD([sQuery(id+"F6.wireOp",EDGE,"E31")])]}),makeQuery(id+"F24.opExtrude","SWEPT_FACE",FACE,{"disambiguationData":[OSD([sQuery(id+"F23.wireOp",EDGE,"E65.filletArc")])]})]})});
            var Q34;
            Q34=makeQuery(id+"F26.opBoolean","COPY",EDGE,{"derivedFrom":makeQuery(id+"F25.opBoolean","INTERSECT",EDGE,{"derivedFrom":[makeQuery(id+"F7.opExtrude","SWEPT_FACE",FACE,{"disambiguationData":[OSD([sQuery(id+"F6.wireOp",EDGE,"E31")])]}),makeQuery(id+"F24.opExtrude","SWEPT_FACE",FACE,{"disambiguationData":[OSD([sQuery(id+"F23.wireOp",EDGE,"E53")])]})]})});
            var Q35;
            Q35=makeQuery(id+"F26.opBoolean","COPY",EDGE,{"derivedFrom":makeQuery(id+"F25.opBoolean","INTERSECT",EDGE,{"derivedFrom":[makeQuery(id+"F7.opExtrude","SWEPT_FACE",FACE,{"disambiguationData":[OSD([sQuery(id+"F6.wireOp",EDGE,"E31")])]}),makeQuery(id+"F24.opExtrude","SWEPT_FACE",FACE,{"disambiguationData":[OSD([sQuery(id+"F23.wireOp",EDGE,"E66.filletArc")])]})]})});
            var Q36;
            Q36=makeQuery(id+"F26.opBoolean","COPY",EDGE,{"derivedFrom":makeQuery(id+"F25.opBoolean","INTERSECT",EDGE,{"derivedFrom":[makeQuery(id+"F7.opExtrude","SWEPT_FACE",FACE,{"disambiguationData":[OSD([sQuery(id+"F6.wireOp",EDGE,"E31")])]}),makeQuery(id+"F24.opExtrude","SWEPT_FACE",FACE,{"disambiguationData":[OSD([sQuery(id+"F23.wireOp",EDGE,"E67.filletArc")])]})]})});
            var Q37;
            Q37=makeQuery(id+"F26.opBoolean","COPY",EDGE,{"derivedFrom":makeQuery(id+"F25.opBoolean","INTERSECT",EDGE,{"derivedFrom":[makeQuery(id+"F7.opExtrude","SWEPT_FACE",FACE,{"disambiguationData":[OSD([sQuery(id+"F6.wireOp",EDGE,"E31")])]}),makeQuery(id+"F24.opExtrude","SWEPT_FACE",FACE,{"disambiguationData":[OSD([sQuery(id+"F23.wireOp",EDGE,"E55")])]})]})});
            var Q38;
            Q38=makeQuery(id+"F26.opBoolean","COPY",EDGE,{"derivedFrom":makeQuery(id+"F25.opBoolean","INTERSECT",EDGE,{"derivedFrom":[makeQuery(id+"F7.opExtrude","SWEPT_FACE",FACE,{"disambiguationData":[OSD([sQuery(id+"F6.wireOp",EDGE,"E31")])]}),makeQuery(id+"F24.opExtrude","SWEPT_FACE",FACE,{"disambiguationData":[OSD([sQuery(id+"F23.wireOp",EDGE,"E68.filletArc")])]})]})});
            var Q39;
            Q39=makeQuery(id+"F26.opBoolean","COPY",EDGE,{"derivedFrom":makeQuery(id+"F25.opBoolean","INTERSECT",EDGE,{"derivedFrom":[makeQuery(id+"F7.opExtrude","SWEPT_FACE",FACE,{"disambiguationData":[OSD([sQuery(id+"F6.wireOp",EDGE,"E31")])]}),makeQuery(id+"F24.opExtrude","SWEPT_FACE",FACE,{"disambiguationData":[OSD([sQuery(id+"F23.wireOp",EDGE,"E69.filletArc")])]})]})});
            var Q40;
            Q40=makeQuery(id+"F26.opBoolean","COPY",EDGE,{"derivedFrom":makeQuery(id+"F25.opBoolean","INTERSECT",EDGE,{"derivedFrom":[makeQuery(id+"F7.opExtrude","SWEPT_FACE",FACE,{"disambiguationData":[OSD([sQuery(id+"F6.wireOp",EDGE,"E31")])]}),makeQuery(id+"F24.opExtrude","SWEPT_FACE",FACE,{"disambiguationData":[OSD([sQuery(id+"F23.wireOp",EDGE,"E57")])]})]})});
            var Q41;
            Q41=makeQuery(id+"F26.opBoolean","COPY",EDGE,{"derivedFrom":makeQuery(id+"F25.opBoolean","INTERSECT",EDGE,{"derivedFrom":[makeQuery(id+"F7.opExtrude","SWEPT_FACE",FACE,{"disambiguationData":[OSD([sQuery(id+"F6.wireOp",EDGE,"E31")])]}),makeQuery(id+"F24.opExtrude","SWEPT_FACE",FACE,{"disambiguationData":[OSD([sQuery(id+"F23.wireOp",EDGE,"E70.filletArc")])]})]})});
            var Q42;
            Q42=makeQuery(id+"F26.opBoolean","COPY",EDGE,{"derivedFrom":makeQuery(id+"F25.opBoolean","INTERSECT",EDGE,{"derivedFrom":[makeQuery(id+"F7.opExtrude","SWEPT_FACE",FACE,{"disambiguationData":[OSD([sQuery(id+"F6.wireOp",EDGE,"E31")])]}),makeQuery(id+"F24.opExtrude","SWEPT_FACE",FACE,{"disambiguationData":[OSD([sQuery(id+"F23.wireOp",EDGE,"E58")])]})]})});
            var Q43;
            Q43=makeQuery(id+"F26.opBoolean","COPY",EDGE,{"derivedFrom":makeQuery(id+"F25.opBoolean","INTERSECT",EDGE,{"derivedFrom":[makeQuery(id+"F7.opExtrude","SWEPT_FACE",FACE,{"disambiguationData":[OSD([sQuery(id+"F6.wireOp",EDGE,"E31")])]}),makeQuery(id+"F24.opExtrude","SWEPT_FACE",FACE,{"disambiguationData":[OSD([sQuery(id+"F23.wireOp",EDGE,"E71.filletArc")])]})]})});
            var Q44;
            Q44=makeQuery(id+"F26.opBoolean","COPY",EDGE,{"derivedFrom":makeQuery(id+"F25.opBoolean","INTERSECT",EDGE,{"derivedFrom":[makeQuery(id+"F7.opExtrude","SWEPT_FACE",FACE,{"disambiguationData":[OSD([sQuery(id+"F6.wireOp",EDGE,"E31")])]}),makeQuery(id+"F24.opExtrude","SWEPT_FACE",FACE,{"disambiguationData":[OSD([sQuery(id+"F23.wireOp",EDGE,"E52")])]})]})});
            var Q45;
            Q45=makeQuery(id+"F26.opBoolean","COPY",EDGE,{"derivedFrom":makeQuery(id+"F25.opBoolean","INTERSECT",EDGE,{"derivedFrom":[makeQuery(id+"F7.opExtrude","SWEPT_FACE",FACE,{"disambiguationData":[OSD([sQuery(id+"F6.wireOp",EDGE,"E31")])]}),makeQuery(id+"F24.opExtrude","SWEPT_FACE",FACE,{"disambiguationData":[OSD([sQuery(id+"F23.wireOp",EDGE,"E56")])]})]})});
            var Q46;
            Q46=makeQuery(id+"F26.opBoolean","COPY",EDGE,{"derivedFrom":makeQuery(id+"F25.opBoolean","INTERSECT",EDGE,{"derivedFrom":[makeQuery(id+"F7.opExtrude","SWEPT_FACE",FACE,{"disambiguationData":[OSD([sQuery(id+"F6.wireOp",EDGE,"E31")])]}),makeQuery(id+"F24.opExtrude","SWEPT_FACE",FACE,{"disambiguationData":[OSD([sQuery(id+"F23.wireOp",EDGE,"E54")])]})]})});
            var Q47;
            Q47=makeQuery(id+"F26.opBoolean","COPY",EDGE,{"derivedFrom":makeQuery(id+"F25.opBoolean","INTERSECT",EDGE,{"derivedFrom":[makeQuery(id+"F7.opExtrude","SWEPT_FACE",FACE,{"disambiguationData":[OSD([sQuery(id+"F6.wireOp",EDGE,"E31")])]}),makeQuery(id+"F24.opExtrude","SWEPT_FACE",FACE,{"disambiguationData":[OSD([sQuery(id+"F23.wireOp",EDGE,"E50")])]})]})});
            fillet(context, id + "F27", {"entities" : qUnion([Q0, Q1, Q2, Q3, Q4, Q5, Q6, Q7, Q8, Q9, Q10, Q11, Q12, Q13, Q14, Q15, Q16, Q17, Q18, Q19, Q20, Q21, Q22, Q23, Q24, Q25, Q26, Q27, Q28, Q29, Q30, Q31, Q32, Q33, Q34, Q35, Q36, Q37, Q38, Q39, Q40, Q41, Q42, Q43, Q44, Q45, Q46, Q47]), "radius" : 0.5 * mm, "tangentPropagation" : true, "allowEdgeOverflow" : false});
        }
        {
            var Q0;
            Q0=makeQuery(id+"F1.opExtrude","CAP_FACE",FACE,{"disambiguationData":[OSD([sQuery(id+"F0.wireOp",EDGE,"E0")])],"isStart":false});
            extrude(context, id + "F28", {"entities" : qUnion([Q0]), "operationType" : NewBodyOperationType.ADD, "depth" : 3.8 * mm});
        }
        {
            var Q0;
            Q0=makeQuery(id+"F28.opExtrude","CAP_FACE",FACE,{"disambiguationData":[OSD([sQuery(id+"F0.wireOp",EDGE,"E0")])],"isStart":false});
            var sketch = newSketch(context, id + "F29", { "sketchPlane" : qUnion([Q0])});
            skCircle(sketch, "E72", {"center": v(0, 11.43) * mm, "radius": 2.54 * mm});
            skSolve(sketch);
        }
        {
            var Q0;
            Q0 = qSketchRegion(id + "F29", true);
            extrude(context, id + "F30", {"entities" : qUnion([Q0]), "operationType" : NewBodyOperationType.ADD, "depth" : 25.4 * mm});
        }
    });
